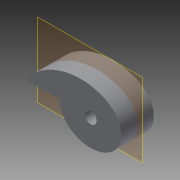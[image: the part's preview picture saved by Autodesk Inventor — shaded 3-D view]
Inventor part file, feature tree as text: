
AUTODESK INVENTOR PART (.ipt)
format: ipt  version: 2014 (Build 180170000, 170)  size: 99,840 bytes
history: native  units: in
note: dims shown in document units (in); Inventor stores cm internally (conversion verified against a paired STEP export)
features: extrude x1, sketch x1
ambient origin geometry x8: Origin, YZ Plane, XZ Plane, XY Plane, X Axis, Y Axis, Z Axis, Center Point
bodies: Solid1 (feature_tree)
feature tree (2):
  extrude  "Extrusion1"  Depth=0.95in
  sketch  "Sketch1"  dims[d42=1.252in d43=1.9803in d44=0.949in d45=1.2135in d46=0.4555in d47=1.5659in d48=0.8021in d53=0.8623in d57=0.2344in d62=0.95in d63=0.8215in d64=0.375in d65=1.0in d66=0.0in]
